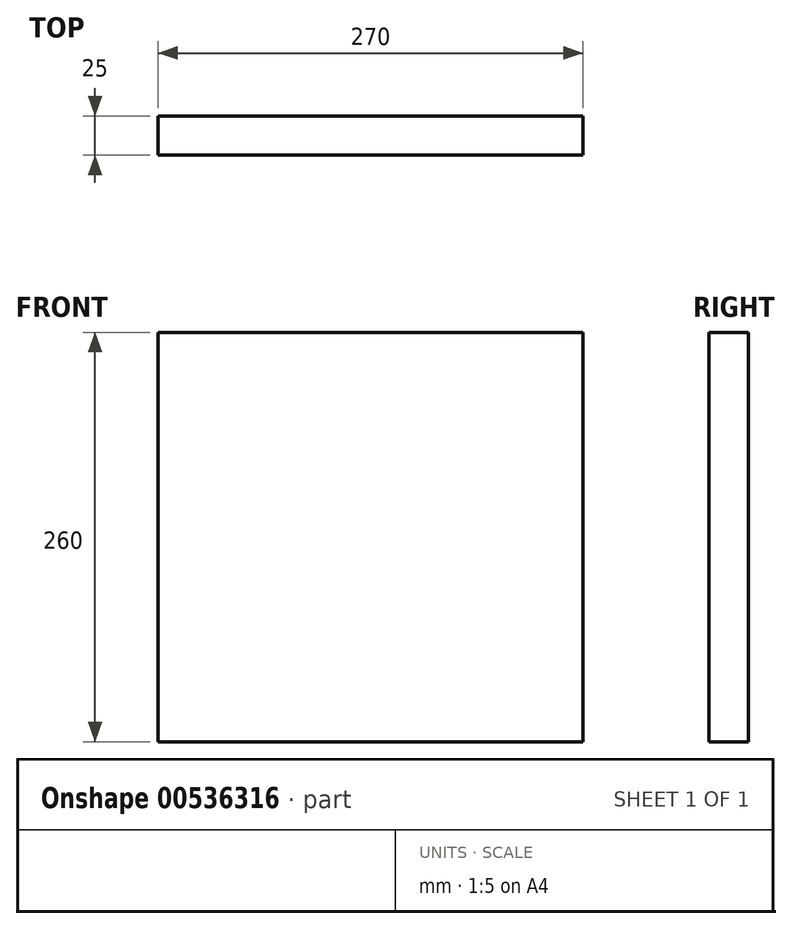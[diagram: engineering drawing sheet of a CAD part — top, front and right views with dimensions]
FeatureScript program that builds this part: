
annotation { "Feature Type Name" : "Feature", "Feature Type Description" : "" }
export const myFeature = defineFeature(function(context is Context, id is Id, definition is map)
    precondition{}
    {
        {
            var Q0;
            Q0=qCreatedBy(makeId("Front.planeOp"),FACE);
            var sketch = newSketch(context, id + "F0", { "sketchPlane" : qUnion([Q0])});
            skLineSegment(sketch, "E0.bottom", {"start": v(0, 0) * mm, "end": v(270, 0) * mm});
            skLineSegment(sketch, "E0.top", {"start": v(0, 260) * mm, "end": v(270, 260) * mm});
            skLineSegment(sketch, "E0.left", {"start": v(0, 0) * mm, "end": v(0, 260) * mm});
            skLineSegment(sketch, "E0.right", {"start": v(270, 0) * mm, "end": v(270, 260) * mm});
            skSolve(sketch);
        }
        {
            var Q0;
            Q0=makeQuery(id+"F0.imprint","IMPRINT",FACE,{"disambiguationData":[TD([[makeQuery(id+"F0.imprint","IMPRINT",EDGE,{"derivedFrom":sQuery(id+"F0.wireOp",EDGE,"E0.bottom")}),1.0]])]});
            extrude(context, id + "F1", {"entities" : qUnion([Q0]), "depth" : 25 * mm, "offsetDistance" : 25 * mm});
        }
    });
